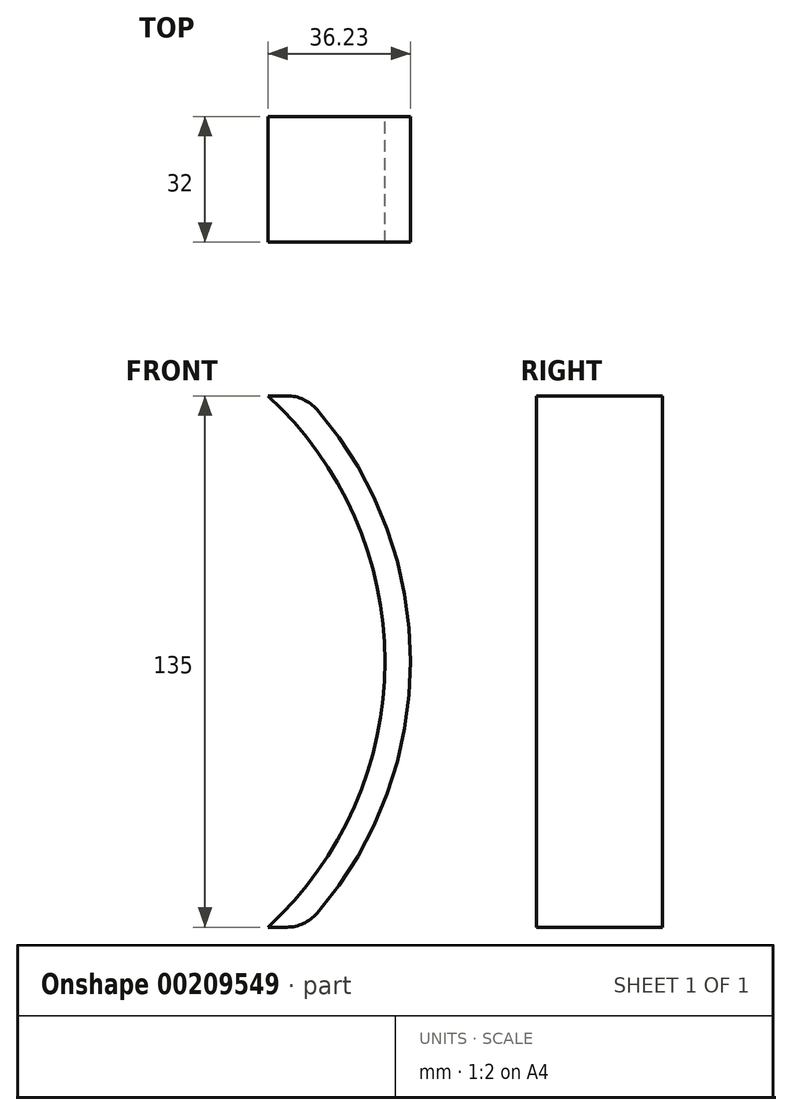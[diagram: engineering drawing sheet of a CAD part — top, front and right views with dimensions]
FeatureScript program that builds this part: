
annotation { "Feature Type Name" : "Feature", "Feature Type Description" : "" }
export const myFeature = defineFeature(function(context is Context, id is Id, definition is map)
    precondition{}
    {
        {
            var Q0;
            Q0=qCreatedBy(makeId("Front.planeOp"),FACE);
            var sketch = newSketch(context, id + "F0", { "sketchPlane" : qUnion([Q0])});
            skArc(sketch, "E0", {"start": v(61.77, -67.5) * mm, "mid": v(91.5, 0) * mm, "end": v(61.77, 67.5) * mm});
            skLineSegment(sketch, "E1", {"start": v(61.77, 67.5) * mm, "end": v(61.77, -67.5) * mm, "construction": true});
            skArc(sketch, "E2", {"start": v(74.19, -64.03) * mm, "mid": v(98, 0) * mm, "end": v(74.19, 64.03) * mm});
            skLineSegment(sketch, "E3", {"start": v(61.77, 67.5) * mm, "end": v(66.62, 67.5) * mm});
            skLineSegment(sketch, "E4", {"start": v(61.77, -67.5) * mm, "end": v(66.62, -67.5) * mm});
            skPoint(sketch, "E5.visualSharp", {"position": v(71.05, 67.5) * mm});
            skArc(sketch, "E5.filletArc", {"start": v(74.19, 64.03) * mm, "mid": v(70.78, 66.6) * mm, "end": v(66.62, 67.5) * mm});
            skPoint(sketch, "E6.visualSharp", {"position": v(71.05, -67.5) * mm});
            skArc(sketch, "E6.filletArc", {"start": v(66.62, -67.5) * mm, "mid": v(70.78, -66.6) * mm, "end": v(74.19, -64.03) * mm});
            skSolve(sketch);
        }
        {
            var Q0;
            Q0 = qSketchRegion(id + "F0", true);
            extrude(context, id + "F1", {"entities" : qUnion([Q0]), "depth" : 32 * mm});
        }
    });
